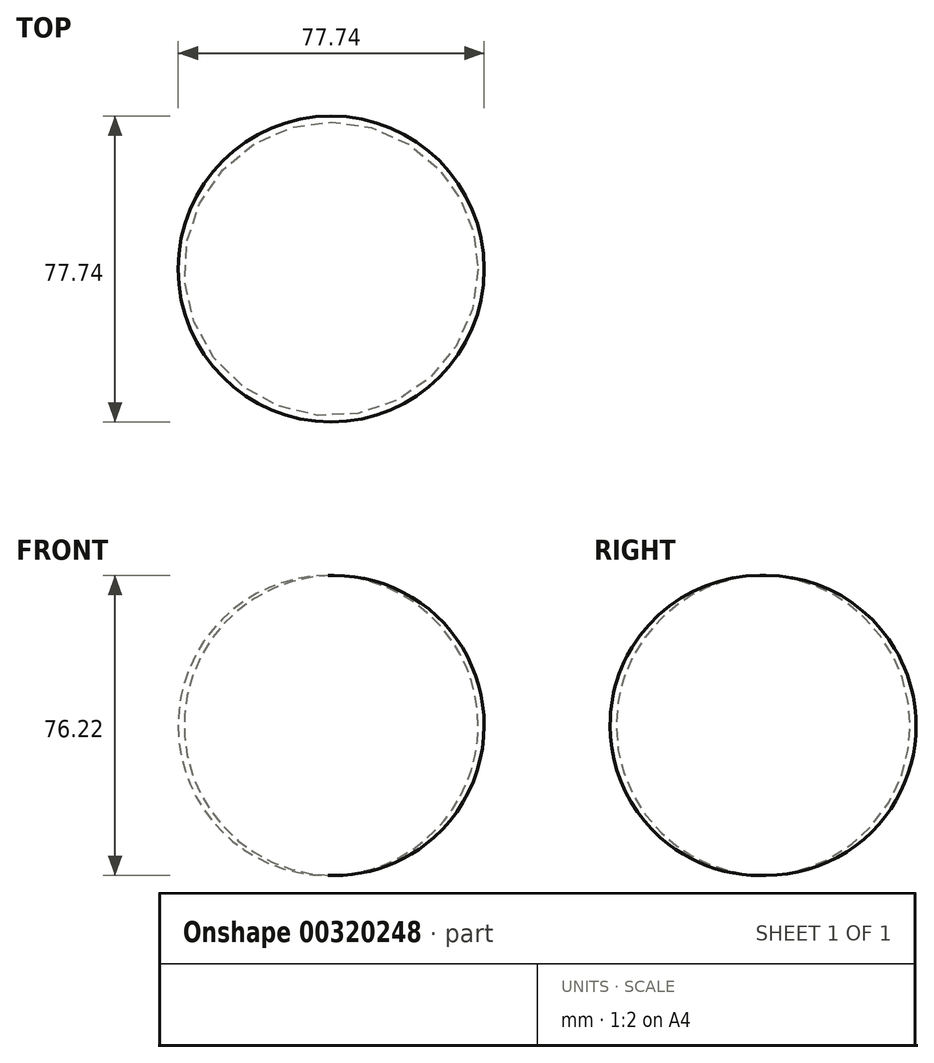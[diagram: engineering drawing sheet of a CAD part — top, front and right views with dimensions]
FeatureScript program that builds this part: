
annotation { "Feature Type Name" : "Feature", "Feature Type Description" : "" }
export const myFeature = defineFeature(function(context is Context, id is Id, definition is map)
    precondition{}
    {
        {
            var Q0;
            Q0=qCreatedBy(makeId("Front.planeOp"),FACE);
            var sketch = newSketch(context, id + "F0", { "sketchPlane" : qUnion([Q0])});
            skLineSegment(sketch, "E0", {"start": v(0, 0) * mm, "end": v(0, 50.8) * mm});
            skArc(sketch, "E1", {"start": v(0, 0) * mm, "mid": v(25.4, 25.4) * mm, "end": v(0, 50.8) * mm});
            skSolve(sketch);
        }
        {
            var Q0;
            Q0 = qSketchRegion(id + "F0", true);
            var Q1;
            Q1=sQuery(id+"F0.wireOp",EDGE,"E0");
            revolve(context, id + "F1", {"entities" : qUnion([Q0]), "axis" : qUnion([Q1]), "revolveType" : RevolveType.FULL});
        }
        {
            var Q0;
            Q0=qCreatedBy(makeId("Front.planeOp"),FACE);
            var sketch = newSketch(context, id + "F2", { "sketchPlane" : qUnion([Q0])});
            skLineSegment(sketch, "E2", {"start": v(0, 0) * mm, "end": v(0, 76.2) * mm});
            skArc(sketch, "E3", {"start": v(0, 0) * mm, "mid": v(38.87, 38.1) * mm, "end": v(0, 76.2) * mm});
            skSolve(sketch);
        }
        {
            var Q0;
            Q0 = qSketchRegion(id + "F2", true);
            var Q1;
            Q1=sQuery(id+"F2.wireOp",EDGE,"E2");
            revolve(context, id + "F3", {"operationType" : NewBodyOperationType.ADD, "entities" : qUnion([Q0]), "axis" : qUnion([Q1]), "revolveType" : RevolveType.FULL});
        }
    });
